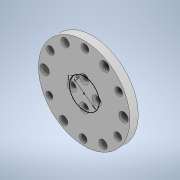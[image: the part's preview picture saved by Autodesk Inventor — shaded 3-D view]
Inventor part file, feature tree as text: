
AUTODESK INVENTOR PART (.ipt)
format: ipt  version: 2020 (Build 240168000, 168)  size: 221,696 bytes
history: native  units: mm
features: reference x12, sketch x5, other x5, extrude x3, fillet x1, hole x1
ambient origin geometry x8: Origin, YZ Plane, XZ Plane, XY Plane, X Axis, Y Axis, Z Axis, Center Point
bodies: Solid1 (feature_tree)
feature tree (27):
  extrude  "Extrusion1"  Depth=2.0mm TaperAngle=0.0deg
  extrude  "Extrusion2"  Depth=5.0mm TaperAngle=0.0deg
  fillet  "Fillet1"  Radius=5.0mm
  extrude  "Extrusion3"  Depth=10.0mm
  sketch  "Sketch4"  dims[d12=15.0mm]
  hole  "Hole2"  [1 undecoded]
  sketch  "Sketch1"  dims[d0=35.0mm d1=2.0mm d2=0.0mm]
  sketch  "Sketch2"  dims[d3=55.0mm d4=5.0mm d5=0.0mm d6=5.0mm]
  sketch  "Sketch3"  dims[d7=10.0mm d8=0.0mm d9=17.9mm]
  reference  "Reference3"
  reference  "Reference4"
  reference  "Reference5"
  reference  "Reference6"
  reference  "Reference7"
  reference  "Reference8"
  reference  "Reference9"
  reference  "Reference10"
  reference  "Reference11"
  reference  "Reference12"
  reference  "Reference13"
  reference  "Reference14"
  sketch  "Sketch5"  dims[d20=2.9mm d21=6.0mm d22=5.5mm d23=2.0mm d24=90.0deg d25=20.0mm d26=0.0mm]
  other  "<userpath>\Desktop\KangKangBalancing\KangKang.iam"
  other  "KangKang.iam"
  other  "100mm-Plastic-Omni-Wheel:1"
  other  "A1_ASM_20"
  other  "F2_19"
note: 1 required parameter value undecoded (feature->parameter linkage not recoverable at this tier; creation-order binding heuristic only, values carry confidence <= 0.55)
